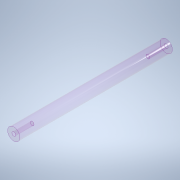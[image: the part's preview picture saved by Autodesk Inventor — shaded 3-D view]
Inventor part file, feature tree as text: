
AUTODESK INVENTOR PART (.ipt)
format: ipt  version: 2020.2 (Build 242310000, 310)  size: 114,688 bytes
history: native  units: mm
features: sketch x3, hole x2, other x1, extrude x1, projected_geometry x1
ambient origin geometry x8: Origin, YZ Plane, XZ Plane, XY Plane, X Axis, Y Axis, Z Axis, Center Point
bodies: Body1 (feature_tree)
feature tree (8):
  other  "ソリッド1"
  extrude  "押し出し1"  Depth=8.0mm
  hole  "穴1"  [1 undecoded]
  hole  "穴2"  [1 undecoded]
  sketch  "スケッチ1"
  sketch  "スケッチ2"
  projected_geometry  "投影ループ1"
  sketch  "スケッチ3"
note: 2 required parameter values undecoded (feature->parameter linkage not recoverable at this tier; creation-order binding heuristic only, values carry confidence <= 0.55)
